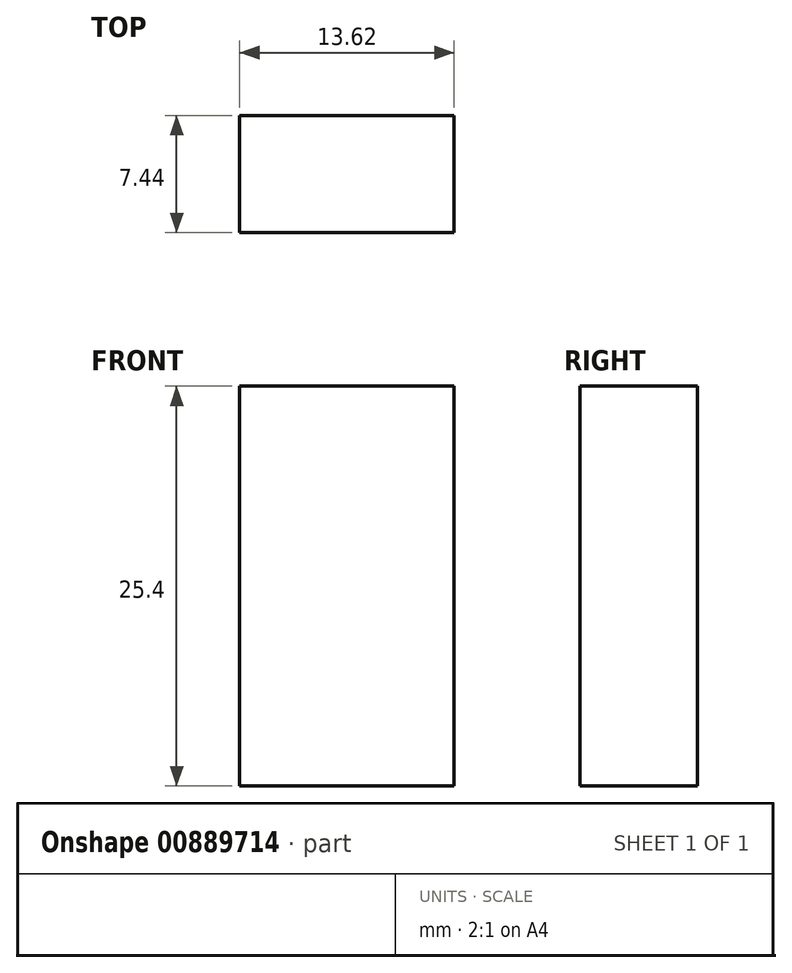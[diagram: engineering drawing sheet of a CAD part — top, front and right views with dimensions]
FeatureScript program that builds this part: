
annotation { "Feature Type Name" : "Feature", "Feature Type Description" : "" }
export const myFeature = defineFeature(function(context is Context, id is Id, definition is map)
    precondition{}
    {
        {
            var Q0;
            Q0=qCreatedBy(makeId("Top.planeOp"),FACE);
            var sketch = newSketch(context, id + "F0", { "sketchPlane" : qUnion([Q0])});
            skLineSegment(sketch, "E0.bottom", {"start": v(-44.87, 13) * mm, "end": v(-31.25, 13) * mm});
            skLineSegment(sketch, "E0.top", {"start": v(-44.87, 20.45) * mm, "end": v(-31.25, 20.45) * mm});
            skLineSegment(sketch, "E0.left", {"start": v(-44.87, 13) * mm, "end": v(-44.87, 20.45) * mm});
            skLineSegment(sketch, "E0.right", {"start": v(-31.25, 13) * mm, "end": v(-31.25, 20.45) * mm});
            skSolve(sketch);
        }
        {
            var Q0;
            Q0 = qSketchRegion(id + "F0", true);
            extrude(context, id + "F1", {"entities" : qUnion([Q0]), "depth" : 25.4 * mm, "offsetDistance" : 25.4 * mm});
        }
    });
